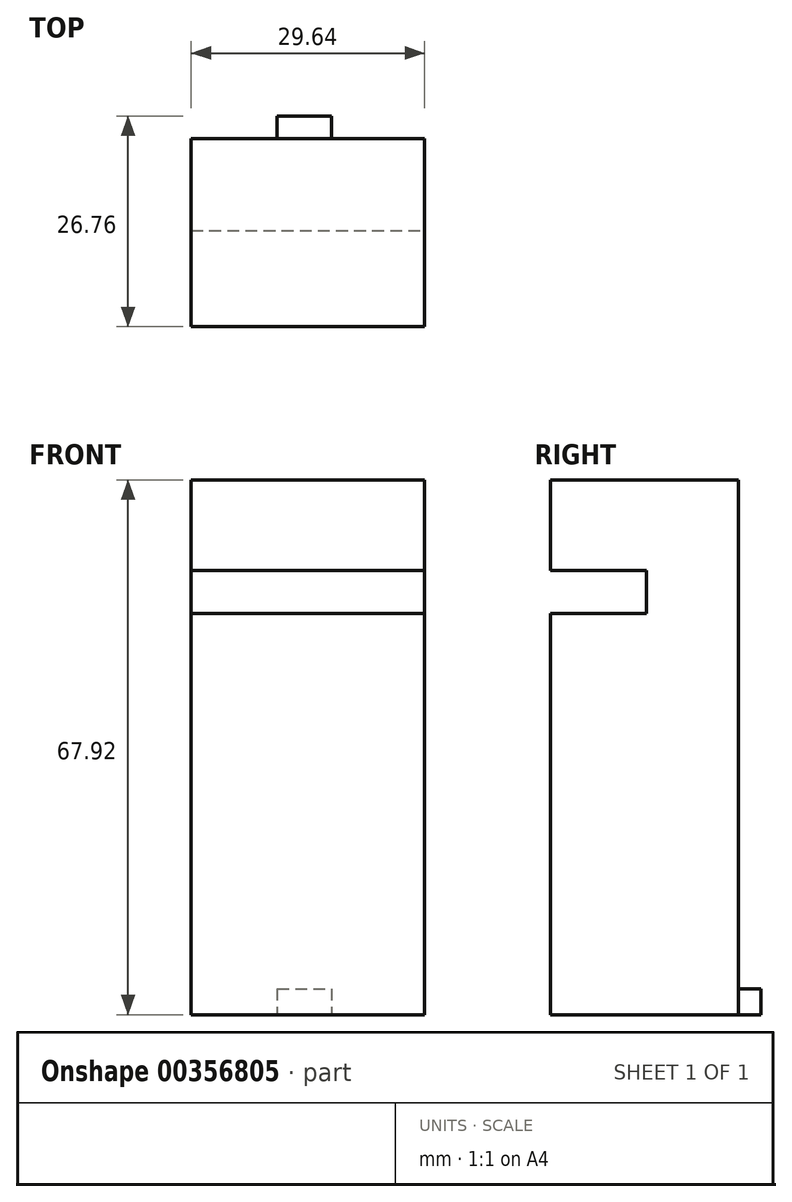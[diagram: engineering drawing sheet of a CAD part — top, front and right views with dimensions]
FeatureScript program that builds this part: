
annotation { "Feature Type Name" : "Feature", "Feature Type Description" : "" }
export const myFeature = defineFeature(function(context is Context, id is Id, definition is map)
    precondition{}
    {
        {
            var Q0;
            Q0=qCreatedBy(makeId("Front.planeOp"),FACE);
            var sketch = newSketch(context, id + "F0", { "sketchPlane" : qUnion([Q0])});
            skLineSegment(sketch, "E0.bottom", {"start": v(0, 0) * mm, "end": v(29.64, 0) * mm});
            skLineSegment(sketch, "E0.top", {"start": v(0, 67.92) * mm, "end": v(29.64, 67.92) * mm});
            skLineSegment(sketch, "E0.left", {"start": v(0, 0) * mm, "end": v(0, 67.92) * mm});
            skLineSegment(sketch, "E0.right", {"start": v(29.64, 0) * mm, "end": v(29.64, 67.92) * mm});
            skSolve(sketch);
        }
        {
            var Q0;
            Q0=makeQuery(id+"F0.imprint","IMPRINT",FACE,{"disambiguationData":[TD([[makeQuery(id+"F0.imprint","IMPRINT",EDGE,{"derivedFrom":sQuery(id+"F0.wireOp",EDGE,"E0.bottom")}),1.0]])]});
            extrude(context, id + "F1", {"entities" : qUnion([Q0]), "depth" : 23.88 * mm});
        }
        {
            var Q0;
            Q0=qCreatedBy(makeId("Front.planeOp"),FACE);
            var sketch = newSketch(context, id + "F2", { "sketchPlane" : qUnion([Q0])});
            skLineSegment(sketch, "E1.bottom", {"start": v(0, 56.4) * mm, "end": v(29.64, 56.4) * mm});
            skLineSegment(sketch, "E1.top", {"start": v(0, 50.94) * mm, "end": v(29.64, 50.94) * mm});
            skLineSegment(sketch, "E1.left", {"start": v(0, 56.4) * mm, "end": v(0, 50.94) * mm});
            skLineSegment(sketch, "E1.right", {"start": v(29.64, 56.4) * mm, "end": v(29.64, 50.94) * mm});
            skSolve(sketch);
        }
        {
            var Q0;
            Q0=makeQuery(id+"F2.imprint","IMPRINT",FACE,{"disambiguationData":[TD([[makeQuery(id+"F2.imprint","IMPRINT",EDGE,{"derivedFrom":sQuery(id+"F2.wireOp",EDGE,"E1.bottom")}),-1.0]])]});
            extrude(context, id + "F3", {"entities" : qUnion([Q0]), "operationType" : NewBodyOperationType.ADD, "depth" : 40.64 * mm});
        }
        {
            var Q0;
            Q0=makeQuery(id+"F3.opExtrude","CAP_FACE",FACE,{"disambiguationData":[OSD([sQuery(id+"F2.wireOp",EDGE,"E1.bottom"),sQuery(id+"F2.wireOp",EDGE,"E1.top"),sQuery(id+"F2.wireOp",EDGE,"E1.left"),sQuery(id+"F2.wireOp",EDGE,"E1.right")])],"isStart":false});
            extrude(context, id + "F4", {"entities" : qUnion([Q0]), "operationType" : NewBodyOperationType.REMOVE, "oppositeDirection" : true, "depth" : 28.96 * mm});
        }
        {
            var Q0;
            Q0=qCreatedBy(makeId("Top.planeOp"),FACE);
            var sketch = newSketch(context, id + "F5", { "sketchPlane" : qUnion([Q0])});
            skLineSegment(sketch, "E2.bottom", {"start": v(10.94, 0) * mm, "end": v(17.84, 0) * mm});
            skLineSegment(sketch, "E2.top", {"start": v(10.94, 2.88) * mm, "end": v(17.84, 2.88) * mm});
            skLineSegment(sketch, "E2.left", {"start": v(10.94, 0) * mm, "end": v(10.94, 2.88) * mm});
            skLineSegment(sketch, "E2.right", {"start": v(17.84, 0) * mm, "end": v(17.84, 2.88) * mm});
            skSolve(sketch);
        }
        {
            var Q0;
            Q0=makeQuery(id+"F5.imprint","IMPRINT",FACE,{"disambiguationData":[TD([[makeQuery(id+"F5.imprint","IMPRINT",EDGE,{"derivedFrom":sQuery(id+"F5.wireOp",EDGE,"E2.bottom")}),1.0]])]});
            extrude(context, id + "F6", {"entities" : qUnion([Q0]), "operationType" : NewBodyOperationType.ADD, "depth" : 3.3 * mm});
        }
    });
